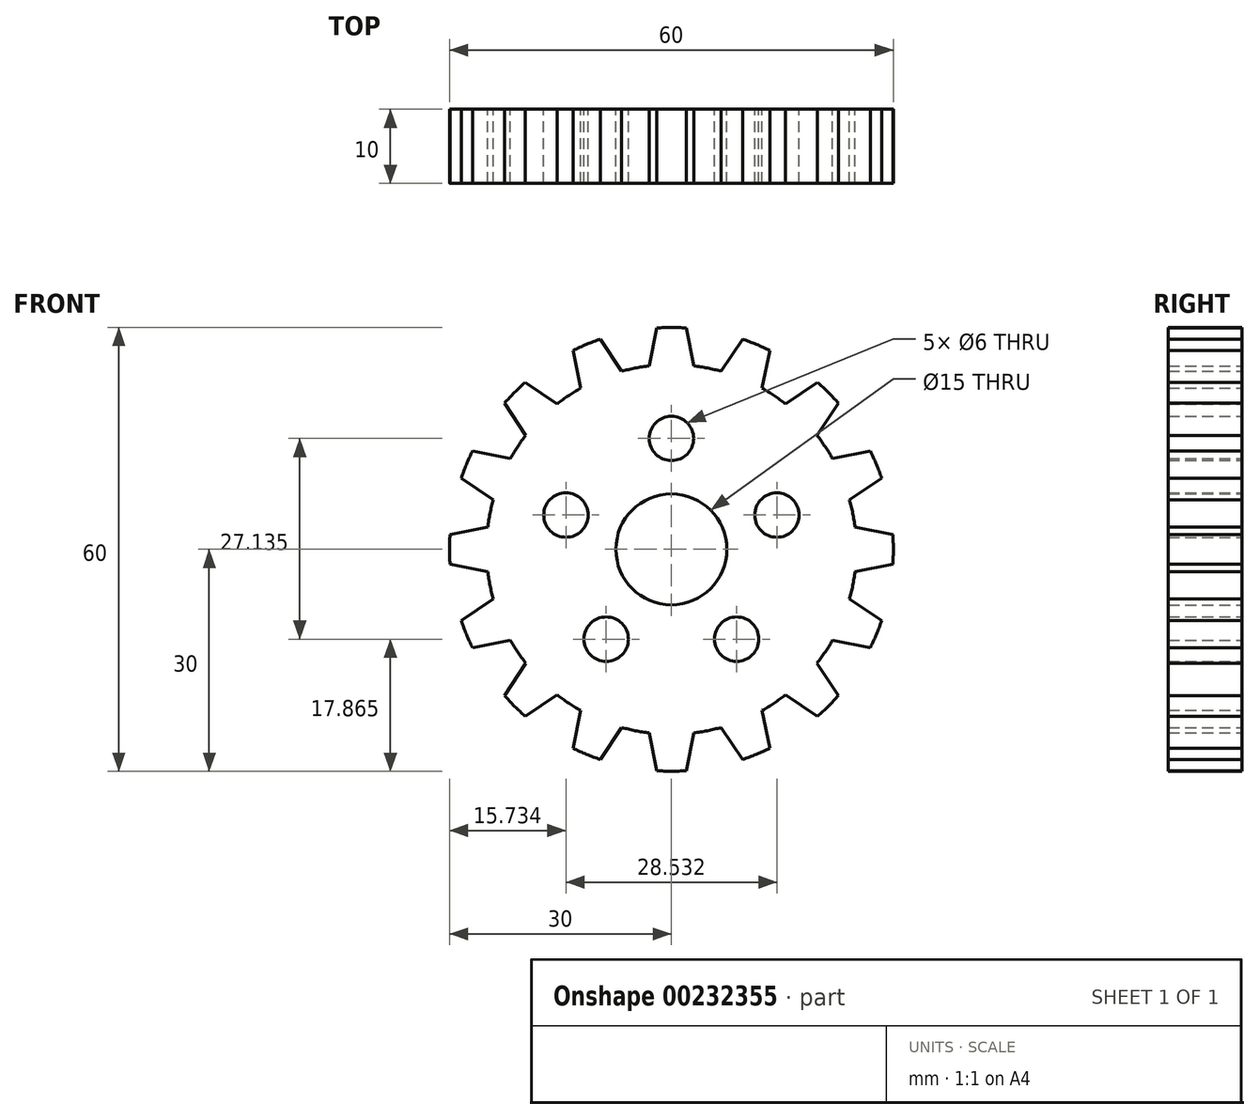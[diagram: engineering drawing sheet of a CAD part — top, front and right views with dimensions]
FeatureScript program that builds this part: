
annotation { "Feature Type Name" : "Feature", "Feature Type Description" : "" }
export const myFeature = defineFeature(function(context is Context, id is Id, definition is map)
    precondition{}
    {
        {
            var Q0;
            Q0=qCreatedBy(makeId("Front.planeOp"),FACE);
            var sketch = newSketch(context, id + "F0", { "sketchPlane" : qUnion([Q0])});
            skCircle(sketch, "E0", {"center": v(0, 0) * mm, "radius": 7.5 * mm});
            skCircle(sketch, "E1", {"center": v(0, 0) * mm, "radius": 15 * mm, "construction": true});
            skArc(sketch, "E2", {"start": v(-12.27, 21.78) * mm, "mid": v(-13.89, 20.79) * mm, "end": v(-15.43, 19.67) * mm});
            skArc(sketch, "E3", {"start": v(2, 29.93) * mm, "mid": v(0, 30) * mm, "end": v(-2, 29.93) * mm});
            skCircle(sketch, "E4", {"center": v(0, 15) * mm, "radius": 3 * mm});
            skLineSegment(sketch, "E5", {"start": v(0, 21) * mm, "end": v(0, 9) * mm, "construction": true});
            skLineSegment(sketch, "E6", {"start": v(-3, 28.53) * mm, "end": v(-3, 20.46) * mm, "construction": true});
            skLineSegment(sketch, "E7", {"start": v(2, 34.55) * mm, "end": v(2, 27.15) * mm, "construction": true});
            skLineSegment(sketch, "E8.MirrorCS", {"start": v(-2, 34.55) * mm, "end": v(-2, 27.15) * mm, "construction": true});
            skLineSegment(sketch, "E9.MirrorCS", {"start": v(3, 28.53) * mm, "end": v(3, 20.46) * mm, "construction": true});
            skLineSegment(sketch, "E10", {"start": v(2, 29.93) * mm, "end": v(3, 24.82) * mm});
            skLineSegment(sketch, "E11", {"start": v(-2, 29.93) * mm, "end": v(-3, 24.82) * mm});
            skArc(sketch, "E12.1.0", {"start": v(-9.6, 28.42) * mm, "mid": v(-11.48, 27.72) * mm, "end": v(-13.3, 26.89) * mm});
            skLineSegment(sketch, "E12.1.1", {"start": v(-13.3, 26.89) * mm, "end": v(-12.27, 21.78) * mm});
            skLineSegment(sketch, "E12.1.2", {"start": v(-9.6, 28.42) * mm, "end": v(-6.73, 24.08) * mm});
            skArc(sketch, "E12.2.0", {"start": v(-19.75, 22.58) * mm, "mid": v(-21.21, 21.21) * mm, "end": v(-22.58, 19.75) * mm});
            skLineSegment(sketch, "E12.2.1", {"start": v(-22.58, 19.75) * mm, "end": v(-19.67, 15.43) * mm});
            skLineSegment(sketch, "E12.2.2", {"start": v(-19.75, 22.58) * mm, "end": v(-15.43, 19.67) * mm});
            skArc(sketch, "E12.3.0", {"start": v(-26.89, 13.3) * mm, "mid": v(-27.72, 11.48) * mm, "end": v(-28.42, 9.6) * mm});
            skLineSegment(sketch, "E12.3.1", {"start": v(-28.42, 9.6) * mm, "end": v(-24.08, 6.73) * mm});
            skLineSegment(sketch, "E12.3.2", {"start": v(-26.89, 13.3) * mm, "end": v(-21.78, 12.27) * mm});
            skArc(sketch, "E12.4.0", {"start": v(-29.93, 2) * mm, "mid": v(-30, 0) * mm, "end": v(-29.93, -2) * mm});
            skLineSegment(sketch, "E12.4.1", {"start": v(-29.93, -2) * mm, "end": v(-24.82, -3) * mm});
            skLineSegment(sketch, "E12.4.2", {"start": v(-29.93, 2) * mm, "end": v(-24.82, 3) * mm});
            skArc(sketch, "E12.5.0", {"start": v(-28.42, -9.6) * mm, "mid": v(-27.72, -11.48) * mm, "end": v(-26.89, -13.3) * mm});
            skLineSegment(sketch, "E12.5.1", {"start": v(-26.89, -13.3) * mm, "end": v(-21.78, -12.27) * mm});
            skLineSegment(sketch, "E12.5.2", {"start": v(-28.42, -9.6) * mm, "end": v(-24.08, -6.73) * mm});
            skArc(sketch, "E12.6.0", {"start": v(-22.58, -19.75) * mm, "mid": v(-21.21, -21.21) * mm, "end": v(-19.75, -22.58) * mm});
            skLineSegment(sketch, "E12.6.1", {"start": v(-19.75, -22.58) * mm, "end": v(-15.43, -19.67) * mm});
            skLineSegment(sketch, "E12.6.2", {"start": v(-22.58, -19.75) * mm, "end": v(-19.67, -15.43) * mm});
            skArc(sketch, "E12.7.0", {"start": v(-13.3, -26.89) * mm, "mid": v(-11.48, -27.72) * mm, "end": v(-9.6, -28.42) * mm});
            skLineSegment(sketch, "E12.7.1", {"start": v(-9.6, -28.42) * mm, "end": v(-6.73, -24.08) * mm});
            skLineSegment(sketch, "E12.7.2", {"start": v(-13.3, -26.89) * mm, "end": v(-12.27, -21.78) * mm});
            skArc(sketch, "E12.8.0", {"start": v(-2, -29.93) * mm, "mid": v(0, -30) * mm, "end": v(2, -29.93) * mm});
            skLineSegment(sketch, "E12.8.1", {"start": v(2, -29.93) * mm, "end": v(3, -24.82) * mm});
            skLineSegment(sketch, "E12.8.2", {"start": v(-2, -29.93) * mm, "end": v(-3, -24.82) * mm});
            skArc(sketch, "E12.9.0", {"start": v(9.6, -28.42) * mm, "mid": v(11.48, -27.72) * mm, "end": v(13.3, -26.89) * mm});
            skLineSegment(sketch, "E12.9.1", {"start": v(13.3, -26.89) * mm, "end": v(12.27, -21.78) * mm});
            skLineSegment(sketch, "E12.9.2", {"start": v(9.6, -28.42) * mm, "end": v(6.73, -24.08) * mm});
            skArc(sketch, "E12.10.0", {"start": v(19.75, -22.58) * mm, "mid": v(21.21, -21.21) * mm, "end": v(22.58, -19.75) * mm});
            skLineSegment(sketch, "E12.10.1", {"start": v(22.58, -19.75) * mm, "end": v(19.67, -15.43) * mm});
            skLineSegment(sketch, "E12.10.2", {"start": v(19.75, -22.58) * mm, "end": v(15.43, -19.67) * mm});
            skArc(sketch, "E12.11.0", {"start": v(26.89, -13.3) * mm, "mid": v(27.72, -11.48) * mm, "end": v(28.42, -9.6) * mm});
            skLineSegment(sketch, "E12.11.1", {"start": v(28.42, -9.6) * mm, "end": v(24.08, -6.73) * mm});
            skLineSegment(sketch, "E12.11.2", {"start": v(26.89, -13.3) * mm, "end": v(21.78, -12.27) * mm});
            skArc(sketch, "E12.12.0", {"start": v(29.93, -2) * mm, "mid": v(30, 0) * mm, "end": v(29.93, 2) * mm});
            skLineSegment(sketch, "E12.12.1", {"start": v(29.93, 2) * mm, "end": v(24.82, 3) * mm});
            skLineSegment(sketch, "E12.12.2", {"start": v(29.93, -2) * mm, "end": v(24.82, -3) * mm});
            skArc(sketch, "E12.13.0", {"start": v(28.42, 9.6) * mm, "mid": v(27.72, 11.48) * mm, "end": v(26.89, 13.3) * mm});
            skLineSegment(sketch, "E12.13.1", {"start": v(26.89, 13.3) * mm, "end": v(21.78, 12.27) * mm});
            skLineSegment(sketch, "E12.13.2", {"start": v(28.42, 9.6) * mm, "end": v(24.08, 6.73) * mm});
            skArc(sketch, "E12.14.0", {"start": v(22.58, 19.75) * mm, "mid": v(21.21, 21.21) * mm, "end": v(19.75, 22.58) * mm});
            skLineSegment(sketch, "E12.14.1", {"start": v(19.75, 22.58) * mm, "end": v(15.43, 19.67) * mm});
            skLineSegment(sketch, "E12.14.2", {"start": v(22.58, 19.75) * mm, "end": v(19.67, 15.43) * mm});
            skArc(sketch, "E12.15.0", {"start": v(13.3, 26.89) * mm, "mid": v(11.48, 27.72) * mm, "end": v(9.6, 28.42) * mm});
            skLineSegment(sketch, "E12.15.1", {"start": v(9.6, 28.42) * mm, "end": v(6.73, 24.08) * mm});
            skLineSegment(sketch, "E12.15.2", {"start": v(13.3, 26.89) * mm, "end": v(12.27, 21.78) * mm});
            skCircle(sketch, "E13.1.0", {"center": v(-14.27, 4.64) * mm, "radius": 3 * mm});
            skCircle(sketch, "E13.2.0", {"center": v(-8.82, -12.14) * mm, "radius": 3 * mm});
            skCircle(sketch, "E13.3.0", {"center": v(8.82, -12.14) * mm, "radius": 3 * mm});
            skCircle(sketch, "E13.4.0", {"center": v(14.27, 4.64) * mm, "radius": 3 * mm});
            skArc(sketch, "E14.trimOffspring", {"start": v(-19.67, 15.43) * mm, "mid": v(-20.79, 13.89) * mm, "end": v(-21.78, 12.27) * mm});
            skArc(sketch, "E15.trimOffspring", {"start": v(-24.08, 6.73) * mm, "mid": v(-24.52, 4.88) * mm, "end": v(-24.82, 3) * mm});
            skArc(sketch, "E16.trimOffspring", {"start": v(-24.82, -3) * mm, "mid": v(-24.52, -4.88) * mm, "end": v(-24.08, -6.73) * mm});
            skArc(sketch, "E17.trimOffspring", {"start": v(-21.78, -12.27) * mm, "mid": v(-20.79, -13.89) * mm, "end": v(-19.67, -15.43) * mm});
            skArc(sketch, "E18.trimOffspring", {"start": v(-15.43, -19.67) * mm, "mid": v(-13.89, -20.79) * mm, "end": v(-12.27, -21.78) * mm});
            skArc(sketch, "E19.trimOffspring", {"start": v(-6.73, -24.08) * mm, "mid": v(-4.88, -24.52) * mm, "end": v(-3, -24.82) * mm});
            skArc(sketch, "E20.trimOffspring", {"start": v(3, -24.82) * mm, "mid": v(4.88, -24.52) * mm, "end": v(6.73, -24.08) * mm});
            skArc(sketch, "E21.trimOffspring", {"start": v(12.27, -21.78) * mm, "mid": v(13.89, -20.79) * mm, "end": v(15.43, -19.67) * mm});
            skArc(sketch, "E22.trimOffspring", {"start": v(19.67, -15.43) * mm, "mid": v(20.79, -13.89) * mm, "end": v(21.78, -12.27) * mm});
            skArc(sketch, "E23.trimOffspring", {"start": v(24.08, -6.73) * mm, "mid": v(24.52, -4.88) * mm, "end": v(24.82, -3) * mm});
            skArc(sketch, "E24.trimOffspring", {"start": v(24.82, 3) * mm, "mid": v(24.52, 4.88) * mm, "end": v(24.08, 6.73) * mm});
            skArc(sketch, "E25.trimOffspring", {"start": v(21.78, 12.27) * mm, "mid": v(20.79, 13.89) * mm, "end": v(19.67, 15.43) * mm});
            skArc(sketch, "E26.trimOffspring", {"start": v(15.43, 19.67) * mm, "mid": v(13.89, 20.79) * mm, "end": v(12.27, 21.78) * mm});
            skArc(sketch, "E27.trimOffspring", {"start": v(6.73, 24.08) * mm, "mid": v(4.88, 24.52) * mm, "end": v(3, 24.82) * mm});
            skArc(sketch, "E28.trimOffspring", {"start": v(-3, 24.82) * mm, "mid": v(-4.88, 24.52) * mm, "end": v(-6.73, 24.08) * mm});
            skSolve(sketch);
        }
        {
            var Q0;
            Q0=makeQuery(id+"F0.imprint","IMPRINT",FACE,{"disambiguationData":[TD([[makeQuery(id+"F0.imprint","IMPRINT",EDGE,{"derivedFrom":sQuery(id+"F0.wireOp",EDGE,"E0")}),-1.0]])]});
            extrude(context, id + "F1", {"entities" : qUnion([Q0]), "depth" : 10 * mm});
        }
    });
